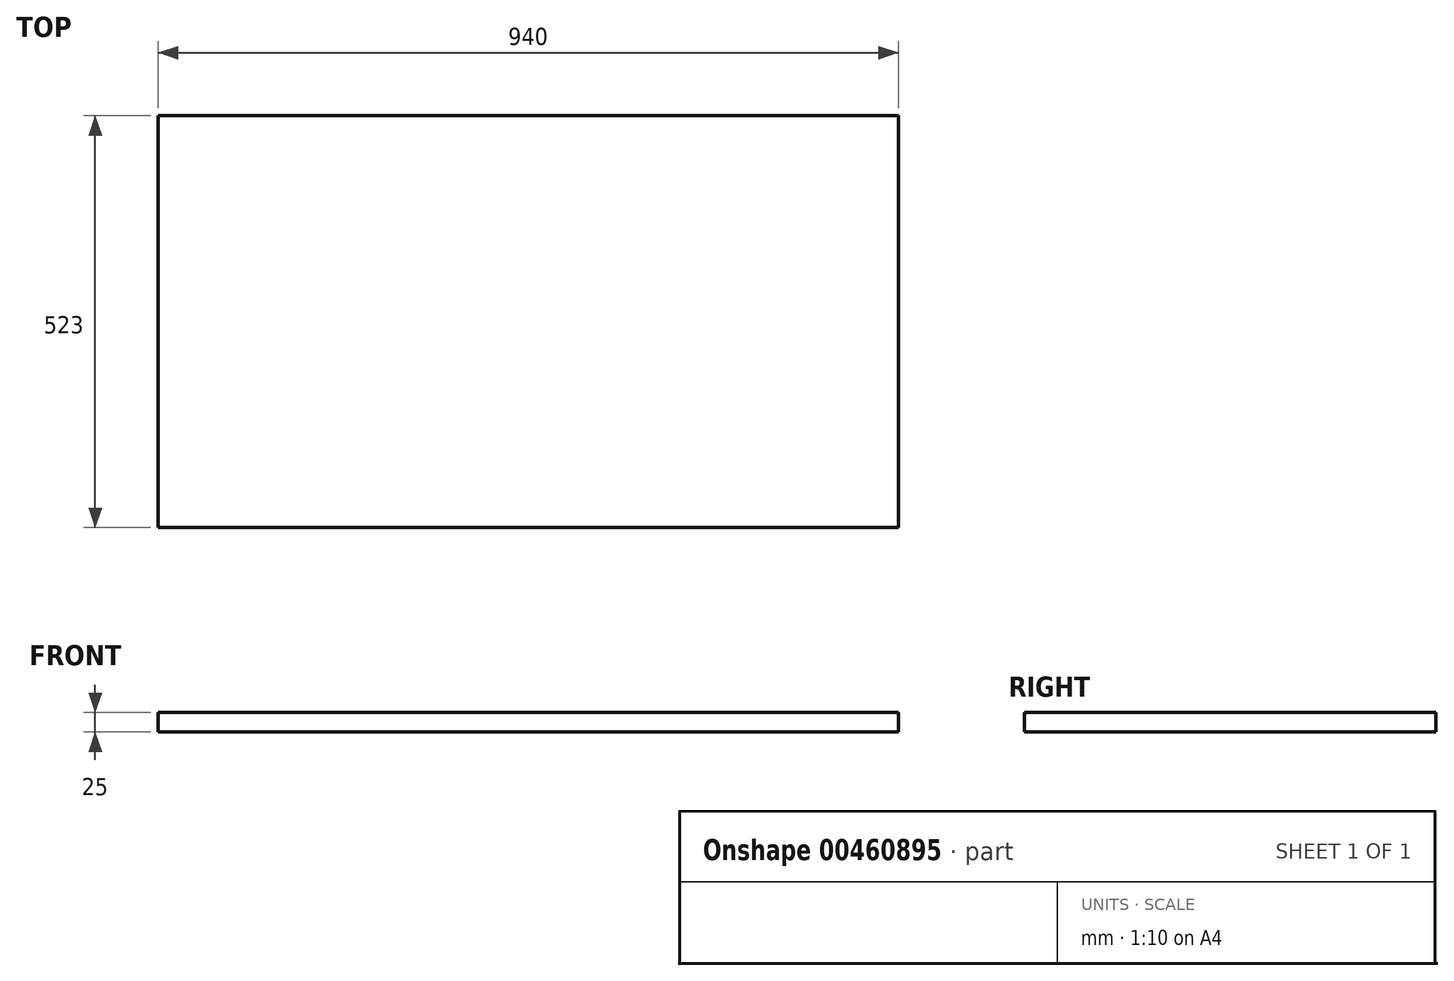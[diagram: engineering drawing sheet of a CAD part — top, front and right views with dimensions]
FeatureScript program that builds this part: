
annotation { "Feature Type Name" : "Feature", "Feature Type Description" : "" }
export const myFeature = defineFeature(function(context is Context, id is Id, definition is map)
    precondition{}
    {
        {
            var Q0;
            Q0=qCreatedBy(makeId("Top.planeOp"),FACE);
            var sketch = newSketch(context, id + "F0", { "sketchPlane" : qUnion([Q0])});
            skLineSegment(sketch, "E0.bottom", {"start": v(-675.4, 175.54) * mm, "end": v(270.6, 175.54) * mm});
            skLineSegment(sketch, "E0.top", {"start": v(-675.4, -353.46) * mm, "end": v(270.6, -353.46) * mm});
            skLineSegment(sketch, "E0.left", {"start": v(-675.4, 175.54) * mm, "end": v(-675.4, -353.46) * mm});
            skLineSegment(sketch, "E0.right", {"start": v(270.6, 175.54) * mm, "end": v(270.6, -353.46) * mm});
            skLineSegment(sketch, "E1.bottom", {"start": v(-672.4, 172.54) * mm, "end": v(267.6, 172.54) * mm});
            skLineSegment(sketch, "E1.top", {"start": v(-672.4, -350.46) * mm, "end": v(267.6, -350.46) * mm});
            skLineSegment(sketch, "E1.left", {"start": v(-672.4, 172.54) * mm, "end": v(-672.4, -350.46) * mm});
            skLineSegment(sketch, "E1.right", {"start": v(267.6, 172.54) * mm, "end": v(267.6, -350.46) * mm});
            skSolve(sketch);
        }
        {
            var Q0;
            Q0=makeQuery(id+"F0.imprint","IMPRINT",FACE,{"disambiguationData":[TD([[makeQuery(id+"F0.imprint","IMPRINT",EDGE,{"derivedFrom":sQuery(id+"F0.wireOp",EDGE,"E1.bottom")}),-1.0]])]});
            extrude(context, id + "F1", {"entities" : qUnion([Q0]), "depth" : 25 * mm});
        }
    });
